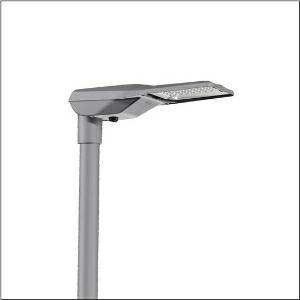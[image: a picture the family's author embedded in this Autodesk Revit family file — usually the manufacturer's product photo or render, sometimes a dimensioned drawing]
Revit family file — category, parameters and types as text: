
# Revit family: streetlight_sl_21_mini___p0_8a_5xe2u33r08hb_8bcd
name_source: partatom
category: Lighting Fixtures
units: mm (PartAtom-declared; Revit-internal decimal feet)

## family parameters
Cut with Voids When Loaded = No
Host = Face
Light Source = No
Part Type = Normal
Room Calculation Point = No
Round Connector Dimension = Use Diameter
Shared = No

## types (1)
- --- (1 x LED, 9120 lm, 66 W, 3000K)
    Apparent Load = 66 VA
    CIE Flux Codes = 33 69 96 100 100
    Color Rendering = 70
    Color Temperature = 3000K
    Default Elevation = 1800 mm
    Description = Streetlight SL 21 mini, mast luminaire, primary light control with lens, of PMMA, primary optical cover: cover, of toughened safety glass, transparent, light distribution: P0.8a, light emission: direct distribution, primary light characteristic: asymmetric, installation type: post-top, side-entry, LED, High Power LED, rated luminous flux: 9.120lm, luminous efficacy: 138lm/W, light colour: 730, colour temperature: 3000K, control gear: D4i, control: pre-setting: logarithmic dimming characteristic, flexible luminous flux parameterisation, time-dependent luminous flux control, constant luminous flux control, overheat protection, mains connection: 220..240V, AC, 50/60Hz, start of lifetime: 66W, end of service life: 69W, reduction: 30W, luminaire housing, of diecast aluminium, powder-coated, Siteco® metallic grey (DB 702S), corrosivity category C5 mid according to DIN EN ISO 12944, multi-level sealing system, sealing non-destructively replaceable, inclination adjustable: 0°, 5°, 10°, 15°, please order mast flange separately, length: 628mm, width: 235mm, height: 110mm, mast flange for spigot size: 42mm (side-entry): 5XC10008XM4, 60/48mm (side-entry/post-top): 5XC10108XM2, 76/60mm (side-entry/post-top): 5XC10108XM1, mounting height: 4..8m, Smart Interface below, protection rating (complete): IP66, insulation class (complete): insulation class II (safety insulation), certification: CE, ENEC, ENEC+, VDE, impact resistance: IK10, permissible operating ambient temperature for outdoor applications: -40..+50°C, standard-compliant lighting for roads and squares, packaging unit: 1 piece

Light Distribution: P0.8a
    Height = 110 mm
    Lamp = 1 x LED
    Lamp Light Flux = 9120 lm
    Lamp Power = 66 W
    Lamp count = 1
    Length = 625 mm
    Luminous efficacy = 138 lm/W
    Manufacturer = Siteco
    ModVariant = No
    Model = 5XE2U33R08HB
    Number of Poles = 1
    OnlyDefault = Yes
    Power Factor = 1
    Product Name = Streetlight SL 21 mini | P0.8a
    Product group = mast luminaire | pylon top
    ProductGroupID = 6100
    Protection Class = Protection class II
    Protection Degree = IP 66
    RLX_Detail_Level = 1
    RLX_Emergency_Light_Flux = 0 lm
    RLX_Emergency_Type = 0
    RLX_Emergency_Type_DB = No
    RlxData = <blob elided: 25917 chars, md5=71f043de>
    Socket = socket
    Standby Power = 0 W
    System Light Flux = 9120 lm
    System Power = 66 W
    Type Comments = factory setting: luminous flux: 100 % | dim-lin: 254 | 670 mA
    Type Image = l_1003516.jpg
    URL = http://relux.com
    VarID = @adj_072550
    Voltage = 0 V
    Weight = 0.00 kg
    Width = 234 mm

## geometry (parser evidence)
native form markers: Blend x4, Sweep x13
no freeform markers — native parametric forms only
